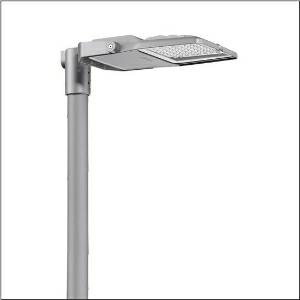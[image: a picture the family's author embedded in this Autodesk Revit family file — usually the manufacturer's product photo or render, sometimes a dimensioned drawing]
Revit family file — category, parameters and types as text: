
# Revit family: floodlight_fl_21_iq_mini___pl33t_5xa7771d4f3a_dbd7
name_source: partatom
category: Lighting Fixtures
units: mm (PartAtom-declared; Revit-internal decimal feet)

## family parameters
Cut with Voids When Loaded = No
Host = Face
Light Source = No
Part Type = Normal
Room Calculation Point = No
Round Connector Dimension = Use Diameter
Shared = No

## types (1)
- --- (1 x LED, 18390 lm, 143 W, 4000K)
    Apparent Load = 143 VA
    CIE Flux Codes = 26 75 99 100 100
    Color Rendering = 70
    Color Temperature = 4000K
    Default Elevation = 1800 mm
    Description = Floodlight FL 21 iQ mini, floodlight, primary light control with lens, of PMMA, primary optical cover: protective disc, of toughened safety glass, transparent, light distribution: PL33T, light emission: direct distribution, installation type: surface-mounted, lamps: LED, High Power LED, rated values: 18.390lm | 143W | 128,6lm/W (begin service life); end service life: 18.390lm | 151,6W; at 50% lumin. flux: 9.195lm | 60,8W | 151,2lm/W, colour temperature: 4000K, colour rendering: CRI > 70, light colour: 740, light setting 1 begin service life: 100% | 18.390lm | 143W | 128,6lm/W | 4.000K, light setting 1 end service life: 151,6W, further light settings possible, control: Auto-Match, Temp-Guard, Lumen-Switch, Night-Set, Smart-Wire, Light-Fading, Desk-Remote (wireless, voltage-free reading and setting of iQ features in the workshop via application-optimized NFC function/RFID function), optimised constant luminous flux control (CLO 2.0), pre-setting: linear dimming characteristic, with terminal, 6-pole, mains connection: 220..240V, AC, 50/60Hz, luminaire housing, of diecast aluminium, powder-coated, SITECO metallic grey (DB 702S), corrosivity category C5 mid according to DIN EN ISO 12944suitable for swimming poolschlorine-resistant, sealing non-destructively replaceable, please order mast flange separately, mast bracket, of steel, galvanised, powder-coated, SITECO metallic grey (DB 702S), protection rating (complete): IP66, insulation class (complete): insulation class II (safety insulation), certification: CE, ENEC, VDE, protection symbol: D, impact resistance: IK08, permissible operating ambient temperature: -40..+40°C, permissible operating ambient temperature for outdoor applications: -40..+50°C, standard: DIN EN 12944, LABS conformity tested according to VDMA 24364:2018-05, packaging unit: 1 piece

Light Distribution: PL33T
    Height = 70 mm
    Lamp = 1 x LED
    Lamp Light Flux = 18390 lm
    Lamp Power = 143 W
    Lamp count = 1
    Length = 485 mm
    Luminous efficacy = 129 lm/W
    Manufacturer = Siteco
    ModVariant = No
    Model = 5XA7771D4F3A
    Number of Poles = 1
    OnlyDefault = Yes
    Power Factor = 1
    Product Name = Floodlight FL 21 iQ mini | PL33T
    Product group = floodlight | pylon annexe
    ProductGroupID = 6201
    Protection Class = Protection class II
    Protection Degree = IP 66
    RLX_Detail_Level = 1
    RLX_Emergency_Light_Flux = 0 lm
    RLX_Emergency_Type = 0
    RLX_Emergency_Type_DB = No
    RlxData = <blob elided: 101709 chars, md5=efd276ab>
    Socket = socket
    Standby Power = 0 W
    System Light Flux = 18390 lm
    System Power = 143 W
    Type Comments = factory setting: luminous flux: 100 % | dim-lin: 254 | 730 mA
    Type Image = l_1007125.jpg
    URL = http://relux.com
    VarID = @adj_148579
    Voltage = 0 V
    Weight = 0.00 kg
    Width = 337 mm

## geometry (parser evidence)
native form markers: Blend x4, Sweep x12
no freeform markers — native parametric forms only
